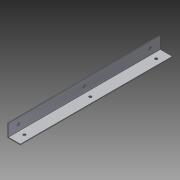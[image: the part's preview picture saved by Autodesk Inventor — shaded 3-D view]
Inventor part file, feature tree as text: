
AUTODESK INVENTOR PART (.ipt)
format: ipt  version: 2014 SP1 (Build 180222100, 222)  size: 101,376 bytes
history: native  units: in
note: dims shown in document units (in); Inventor stores cm internally (conversion verified against a paired STEP export)
features: extrude x3, sketch x3
ambient origin geometry x8: Origin, YZ Plane, XZ Plane, XY Plane, X Axis, Y Axis, Z Axis, Center Point
bodies: Solid1 (feature_tree)
feature tree (6):
  extrude  "Extrusion1"  Depth=0.0312in
  sketch  "Sketch2"  dims[d2=7.5in d3=0.0in d4=0.5in]
  sketch  "Sketch3"  dims[d5=0.125in d6=7.5in d7=1.1811in d9=3.25in d10=0.3937in d12=1.0in d14=0.125in d15=0.5in d16=7.5in d17=1.1811in d19=3.25in d20=0.3937in d22=1.0in d24=1.0in d25=0.0in d26=1.0in d27=0.0in]
  extrude  "Extrusion2"  Depth=7.5in
  extrude  "Extrusion3"  Depth=7.5in
  sketch  "Sketch1"  dims[d0=0.625in d1=0.0312in]
